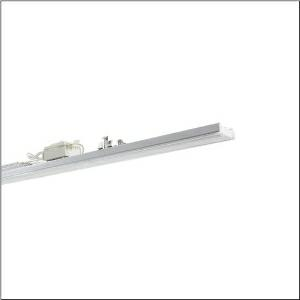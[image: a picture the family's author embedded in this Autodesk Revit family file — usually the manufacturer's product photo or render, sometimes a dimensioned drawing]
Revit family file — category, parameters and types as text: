
# Revit family: licross_r__21_recessed_mo_52tl1ecn485g_7a1e
name_source: partatom
category: Lighting Fixtures
units: mm (PartAtom-declared; Revit-internal decimal feet)

## family parameters
Cut with Voids When Loaded = No
Host = Face
Light Source = No
Part Type = Normal
Room Calculation Point = No
Round Connector Dimension = Use Diameter
Shared = No

## types (1)
- --- (1 x LED, 8960 lm, 49.9 W, 4000K)
    Apparent Load = 50 VA
    CIE Flux Codes = 85 95 99 100 100
    Color Rendering = 80
    Color Temperature = 4000K
    Default Elevation = 1800 mm
    Description = Licross® 21 Recessed MO, luminaire insert, of sheet steel, galvanised, coil coated, white, length: 1.500mm, width: 66mm, height: 67mm, LED rated luminous flux: 8.960lm, light colour: 840, control gear: ON/OFF Multilumen, CLOi, control gear: ECG Multilumen, with plug, 3-pole, with phase selection, mains connection: 220..240V, AC, 50/60Hz, start of lifetime: 50W, end of service life: 61W, halogen-free wiring, primary light control with lens, of plastic, primary optical cover: cover, of PMMA, light emission: direct distribution, primary light characteristic: symmetric, protection rating (complete): IP40, insulation class (complete): insulation class I (protective earthing), certification: CE, ENEC, VDE, UKCA, protection symbol: D if used in an environment without relevant dust loads with corresponding accessories, impact resistance: IK06, permissible ambient temperature for indoor applications: -35..+40°C, corresponds to IFS (International Featured Standards) requirements for safety and quality in the food industry, reducing of maximum allowable ambient temperature of 5°C with ceiling mounting, LABS conformity tested according to VDMA 24364:2018-05, packaging unit: 1 piece
    Height = 58 mm
    Lamp = 1 x LED
    Lamp Light Flux = 8960 lm
    Lamp Power = 49.9 W
    Lamp count = 1
    Length = 1500 mm
    Luminous efficacy = 180 lm/W
    Manufacturer = Siteco
    ModVariant = No
    Model = 52TL1ECN485G
    Mounting Place = Ceiling
    Mounting Type = Pendant
    Number of Poles = 1
    OnlyDefault = Yes
    Power Factor = 1
    Product Name = Licross® 21 Recessed MO
    Product group = luminaire insert
    ProductGroupID = 902
    Protection Class = Protection class I
    Protection Degree = IP 40
    RLX_Detail_Level = 1
    RLX_Emergency_Light_Flux = 0 lm
    RLX_Emergency_Type = 0
    RLX_Emergency_Type_DB = No
    RlxData = <blob elided: 22373 chars, md5=d8ca0505>
    Socket = socket
    Standby Power = 0 W
    System Light Flux = 8960 lm
    System Power = 50 W
    Type Comments = factory setting: luminous flux: 100 % | (A | C | E) | 116 mA
    Type Image = l_1296930.jpg
    URL = http://relux.com
    VarID = @adj_109970
    Voltage = 0 V
    Weight = 0.00 kg
    Width = 66 mm

## geometry (parser evidence)
native form markers: Blend x4, Sweep x10
no freeform markers — native parametric forms only
